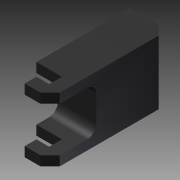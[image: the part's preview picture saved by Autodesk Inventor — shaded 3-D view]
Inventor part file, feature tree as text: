
AUTODESK INVENTOR PART (.ipt)
format: ipt  version: 2015 (Build 190159000, 159)  size: 120,832 bytes
history: native  units: mm
features: extrude x2, hole x1, fillet x1, chamfer x1
ambient origin geometry x8: Origin, YZ Plane, XZ Plane, XY Plane, X Axis, Y Axis, Z Axis, Center Point
bodies: Solid1 (feature_tree)
feature tree (5):
  extrude  "Extrusión1"  Depth=12.0mm
  hole  "Agujero1"  [1 undecoded]
  extrude  "Extrusión2"  Depth=31.3mm
  fillet  "Empalme1"  Radius=4.0mm
  chamfer  "Chaflán1"  Distance=4.0mm
note: 1 required parameter value undecoded (feature->parameter linkage not recoverable at this tier; creation-order binding heuristic only, values carry confidence <= 0.55)
